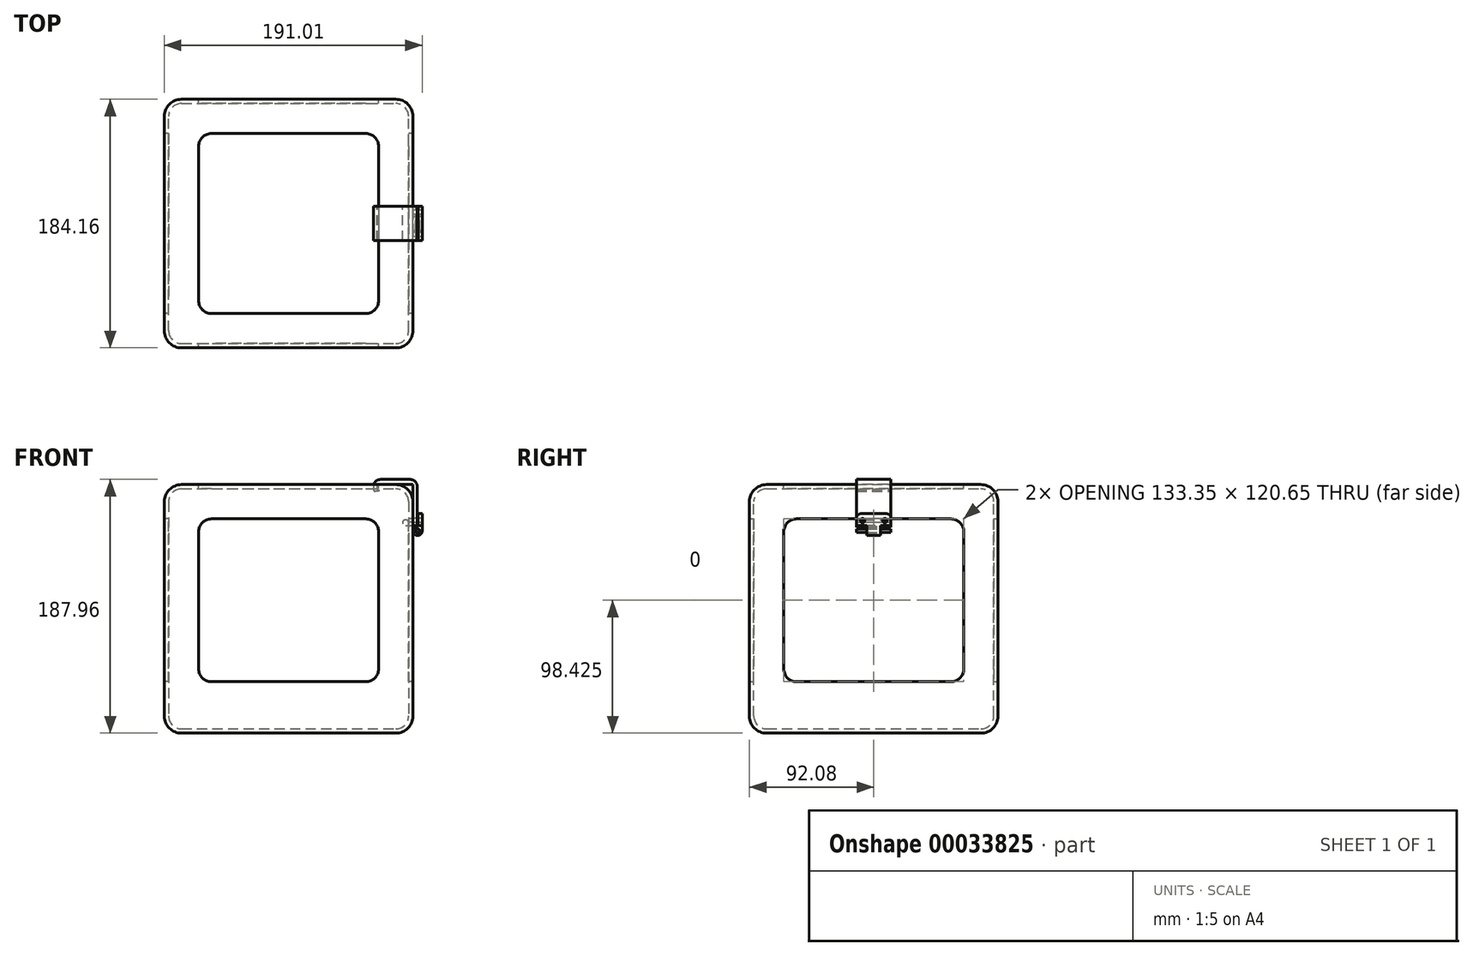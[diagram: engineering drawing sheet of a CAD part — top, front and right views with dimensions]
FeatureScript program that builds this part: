
annotation { "Feature Type Name" : "Feature", "Feature Type Description" : "" }
export const myFeature = defineFeature(function(context is Context, id is Id, definition is map)
    precondition{}
    {
        {
            var Q0;
            Q0=qCreatedBy(makeId("Top.planeOp"),FACE);
            var sketch = newSketch(context, id + "F0", { "sketchPlane" : qUnion([Q0])});
            skLineSegment(sketch, "E0.bottom", {"start": v(-92.08, 92.08) * mm, "end": v(92.08, 92.08) * mm});
            skLineSegment(sketch, "E0.top", {"start": v(-92.08, -92.08) * mm, "end": v(92.08, -92.08) * mm});
            skLineSegment(sketch, "E0.left", {"start": v(-92.08, 92.08) * mm, "end": v(-92.08, -92.08) * mm});
            skLineSegment(sketch, "E0.right", {"start": v(92.08, 92.08) * mm, "end": v(92.08, -92.08) * mm});
            skSolve(sketch);
        }
        {
            var Q0;
            Q0 = qSketchRegion(id + "F0", true);
            extrude(context, id + "F1", {"entities" : qUnion([Q0]), "depth" : 184.15 * mm});
        }
        {
            var Q0;
            Q0=makeQuery(id+"F1.opExtrude","CAP_EDGE",EDGE,{"disambiguationData":[OSD([sQuery(id+"F0.wireOp",EDGE,"E0.top")])],"isStart":false});
            var Q1;
            Q1=makeQuery(id+"F1.opExtrude","CAP_EDGE",EDGE,{"disambiguationData":[OSD([sQuery(id+"F0.wireOp",EDGE,"E0.right")])],"isStart":false});
            var Q2;
            Q2=makeQuery(id+"F1.opExtrude","SWEPT_EDGE",EDGE,{"disambiguationData":[OSD([sQuery(id+"F0.wireOp",EDGE,"E0.top"),sQuery(id+"F0.wireOp",EDGE,"E0.right")])]});
            var Q3;
            Q3=makeQuery(id+"F1.opExtrude","CAP_EDGE",EDGE,{"disambiguationData":[OSD([sQuery(id+"F0.wireOp",EDGE,"E0.left")])],"isStart":false});
            var Q4;
            Q4=makeQuery(id+"F1.opExtrude","SWEPT_EDGE",EDGE,{"disambiguationData":[OSD([sQuery(id+"F0.wireOp",EDGE,"E0.top"),sQuery(id+"F0.wireOp",EDGE,"E0.left")])]});
            var Q5;
            Q5=makeQuery(id+"F1.opExtrude","CAP_EDGE",EDGE,{"disambiguationData":[OSD([sQuery(id+"F0.wireOp",EDGE,"E0.bottom")])],"isStart":false});
            var Q6;
            Q6=makeQuery(id+"F1.opExtrude","SWEPT_EDGE",EDGE,{"disambiguationData":[OSD([sQuery(id+"F0.wireOp",EDGE,"E0.bottom"),sQuery(id+"F0.wireOp",EDGE,"E0.right")])]});
            var Q7;
            Q7=makeQuery(id+"F1.opExtrude","SWEPT_EDGE",EDGE,{"disambiguationData":[OSD([sQuery(id+"F0.wireOp",EDGE,"E0.bottom"),sQuery(id+"F0.wireOp",EDGE,"E0.left")])]});
            var Q8;
            Q8=makeQuery(id+"F1.opExtrude","CAP_EDGE",EDGE,{"disambiguationData":[OSD([sQuery(id+"F0.wireOp",EDGE,"E0.bottom")])],"isStart":true});
            var Q9;
            Q9=makeQuery(id+"F1.opExtrude","CAP_EDGE",EDGE,{"disambiguationData":[OSD([sQuery(id+"F0.wireOp",EDGE,"E0.right")])],"isStart":true});
            var Q10;
            Q10=makeQuery(id+"F1.opExtrude","SWEPT_FACE",FACE,{"disambiguationData":[OSD([sQuery(id+"F0.wireOp",EDGE,"E0.left")])]});
            var Q11;
            Q11=makeQuery(id+"F1.opExtrude","CAP_EDGE",EDGE,{"disambiguationData":[OSD([sQuery(id+"F0.wireOp",EDGE,"E0.top")])],"isStart":true});
            fillet(context, id + "F2", {"entities" : qUnion([Q0, Q1, Q2, Q3, Q4, Q5, Q6, Q7, Q8, Q9, Q10, Q11]), "radius" : 12.7 * mm, "tangentPropagation" : true, "allowEdgeOverflow" : false});
        }
        {
            var Q0;
            Q0=makeQuery(id+"F1.opExtrude","CAP_FACE",FACE,{"disambiguationData":[OSD([sQuery(id+"F0.wireOp",EDGE,"E0.bottom"),sQuery(id+"F0.wireOp",EDGE,"E0.top"),sQuery(id+"F0.wireOp",EDGE,"E0.left"),sQuery(id+"F0.wireOp",EDGE,"E0.right")])],"isStart":false});
            shell(context, id + "F3", {"entities" : qUnion([Q0]), "thickness" : 3.17 * mm});
        }
        {
            var Q0;
            Q0=qCreatedBy(makeId("Right.planeOp"),FACE);
            var sketch = newSketch(context, id + "F4", { "sketchPlane" : qUnion([Q0])});
            skLineSegment(sketch, "E1.bottom", {"start": v(-66.67, 158.75) * mm, "end": v(66.68, 158.75) * mm});
            skLineSegment(sketch, "E1.top", {"start": v(-66.67, 38.1) * mm, "end": v(66.68, 38.1) * mm});
            skLineSegment(sketch, "E1.left", {"start": v(-66.67, 158.75) * mm, "end": v(-66.67, 38.1) * mm});
            skLineSegment(sketch, "E1.right", {"start": v(66.68, 158.75) * mm, "end": v(66.68, 38.1) * mm});
            skSolve(sketch);
        }
        {
            var Q0;
            Q0 = qSketchRegion(id + "F4", true);
            extrude(context, id + "F5", {"entities" : qUnion([Q0]), "operationType" : NewBodyOperationType.REMOVE, "depth" : 127 * mm, "hasSecondDirection" : true, "secondDirectionOppositeDirection" : true, "secondDirectionDepth" : 127 * mm});
        }
        {
            var Q0;
            Q0=qCreatedBy(makeId("Front.planeOp"),FACE);
            var sketch = newSketch(context, id + "F6", { "sketchPlane" : qUnion([Q0])});
            skLineSegment(sketch, "E2.bottom", {"start": v(66.67, 158.75) * mm, "end": v(-66.67, 158.75) * mm});
            skLineSegment(sketch, "E2.top", {"start": v(66.68, 38.1) * mm, "end": v(-66.67, 38.1) * mm});
            skLineSegment(sketch, "E2.left", {"start": v(66.67, 158.75) * mm, "end": v(66.67, 38.1) * mm});
            skLineSegment(sketch, "E2.right", {"start": v(-66.67, 158.75) * mm, "end": v(-66.67, 38.1) * mm});
            skSolve(sketch);
        }
        {
            var Q0;
            Q0 = qSketchRegion(id + "F6", true);
            extrude(context, id + "F7", {"entities" : qUnion([Q0]), "operationType" : NewBodyOperationType.REMOVE, "depth" : 101.6 * mm, "hasSecondDirection" : true, "secondDirectionOppositeDirection" : true, "secondDirectionDepth" : 101.6 * mm});
        }
        {
            var Q0;
            Q0=makeQuery(id+"F7.boolean.opBoolean","COPY",EDGE,{"disambiguationData":[OD(0.0)],"derivedFrom":makeQuery(id+"F7.opExtrude","SWEPT_EDGE",EDGE,{"disambiguationData":[OSD([sQuery(id+"F6.wireOp",EDGE,"E2.bottom"),sQuery(id+"F6.wireOp",EDGE,"E2.left")])]})});
            var Q1;
            Q1=makeQuery(id+"F7.boolean.opBoolean","COPY",EDGE,{"disambiguationData":[OD(0.0)],"derivedFrom":makeQuery(id+"F7.opExtrude","SWEPT_EDGE",EDGE,{"disambiguationData":[OSD([sQuery(id+"F6.wireOp",EDGE,"E2.top"),sQuery(id+"F6.wireOp",EDGE,"E2.left")])]})});
            var Q2;
            Q2=makeQuery(id+"F7.boolean.opBoolean","COPY",EDGE,{"disambiguationData":[OD(0.0)],"derivedFrom":makeQuery(id+"F7.opExtrude","SWEPT_EDGE",EDGE,{"disambiguationData":[OSD([sQuery(id+"F6.wireOp",EDGE,"E2.top"),sQuery(id+"F6.wireOp",EDGE,"E2.right")])]})});
            var Q3;
            Q3=makeQuery(id+"F7.boolean.opBoolean","COPY",EDGE,{"disambiguationData":[OD(0.0)],"derivedFrom":makeQuery(id+"F7.opExtrude","SWEPT_EDGE",EDGE,{"disambiguationData":[OSD([sQuery(id+"F6.wireOp",EDGE,"E2.bottom"),sQuery(id+"F6.wireOp",EDGE,"E2.right")])]})});
            var Q4;
            Q4=makeQuery(id+"F5.boolean.opBoolean","COPY",EDGE,{"disambiguationData":[OD(1.0)],"derivedFrom":makeQuery(id+"F5.opExtrude","SWEPT_EDGE",EDGE,{"disambiguationData":[OSD([sQuery(id+"F4.wireOp",EDGE,"E1.bottom"),sQuery(id+"F4.wireOp",EDGE,"E1.left")])]})});
            var Q5;
            Q5=makeQuery(id+"F5.boolean.opBoolean","COPY",EDGE,{"disambiguationData":[OD(1.0)],"derivedFrom":makeQuery(id+"F5.opExtrude","SWEPT_EDGE",EDGE,{"disambiguationData":[OSD([sQuery(id+"F4.wireOp",EDGE,"E1.bottom"),sQuery(id+"F4.wireOp",EDGE,"E1.right")])]})});
            var Q6;
            Q6=makeQuery(id+"F5.boolean.opBoolean","COPY",EDGE,{"disambiguationData":[OD(1.0)],"derivedFrom":makeQuery(id+"F5.opExtrude","SWEPT_EDGE",EDGE,{"disambiguationData":[OSD([sQuery(id+"F4.wireOp",EDGE,"E1.top"),sQuery(id+"F4.wireOp",EDGE,"E1.left")])]})});
            var Q7;
            Q7=makeQuery(id+"F5.boolean.opBoolean","COPY",EDGE,{"disambiguationData":[OD(1.0)],"derivedFrom":makeQuery(id+"F5.opExtrude","SWEPT_EDGE",EDGE,{"disambiguationData":[OSD([sQuery(id+"F4.wireOp",EDGE,"E1.top"),sQuery(id+"F4.wireOp",EDGE,"E1.right")])]})});
            var Q8;
            Q8=makeQuery(id+"F7.boolean.opBoolean","COPY",EDGE,{"disambiguationData":[OD(1.0)],"derivedFrom":makeQuery(id+"F7.opExtrude","SWEPT_EDGE",EDGE,{"disambiguationData":[OSD([sQuery(id+"F6.wireOp",EDGE,"E2.top"),sQuery(id+"F6.wireOp",EDGE,"E2.left")])]})});
            var Q9;
            Q9=makeQuery(id+"F7.boolean.opBoolean","COPY",EDGE,{"disambiguationData":[OD(1.0)],"derivedFrom":makeQuery(id+"F7.opExtrude","SWEPT_EDGE",EDGE,{"disambiguationData":[OSD([sQuery(id+"F6.wireOp",EDGE,"E2.bottom"),sQuery(id+"F6.wireOp",EDGE,"E2.left")])]})});
            var Q10;
            Q10=makeQuery(id+"F7.boolean.opBoolean","COPY",EDGE,{"disambiguationData":[OD(1.0)],"derivedFrom":makeQuery(id+"F7.opExtrude","SWEPT_EDGE",EDGE,{"disambiguationData":[OSD([sQuery(id+"F6.wireOp",EDGE,"E2.bottom"),sQuery(id+"F6.wireOp",EDGE,"E2.right")])]})});
            var Q11;
            Q11=makeQuery(id+"F7.boolean.opBoolean","COPY",EDGE,{"disambiguationData":[OD(1.0)],"derivedFrom":makeQuery(id+"F7.opExtrude","SWEPT_EDGE",EDGE,{"disambiguationData":[OSD([sQuery(id+"F6.wireOp",EDGE,"E2.top"),sQuery(id+"F6.wireOp",EDGE,"E2.right")])]})});
            var Q12;
            Q12=makeQuery(id+"F5.boolean.opBoolean","COPY",EDGE,{"disambiguationData":[OD(0.0)],"derivedFrom":makeQuery(id+"F5.opExtrude","SWEPT_EDGE",EDGE,{"disambiguationData":[OSD([sQuery(id+"F4.wireOp",EDGE,"E1.top"),sQuery(id+"F4.wireOp",EDGE,"E1.left")])]})});
            var Q13;
            Q13=makeQuery(id+"F5.boolean.opBoolean","COPY",EDGE,{"disambiguationData":[OD(0.0)],"derivedFrom":makeQuery(id+"F5.opExtrude","SWEPT_EDGE",EDGE,{"disambiguationData":[OSD([sQuery(id+"F4.wireOp",EDGE,"E1.bottom"),sQuery(id+"F4.wireOp",EDGE,"E1.left")])]})});
            var Q14;
            Q14=makeQuery(id+"F5.boolean.opBoolean","COPY",EDGE,{"disambiguationData":[OD(0.0)],"derivedFrom":makeQuery(id+"F5.opExtrude","SWEPT_EDGE",EDGE,{"disambiguationData":[OSD([sQuery(id+"F4.wireOp",EDGE,"E1.bottom"),sQuery(id+"F4.wireOp",EDGE,"E1.right")])]})});
            var Q15;
            Q15=makeQuery(id+"F5.boolean.opBoolean","COPY",EDGE,{"disambiguationData":[OD(0.0)],"derivedFrom":makeQuery(id+"F5.opExtrude","SWEPT_EDGE",EDGE,{"disambiguationData":[OSD([sQuery(id+"F4.wireOp",EDGE,"E1.top"),sQuery(id+"F4.wireOp",EDGE,"E1.right")])]})});
            fillet(context, id + "F8", {"entities" : qUnion([Q0, Q1, Q2, Q3, Q4, Q5, Q6, Q7, Q8, Q9, Q10, Q11, Q12, Q13, Q14, Q15]), "radius" : 9.52 * mm, "tangentPropagation" : true, "allowEdgeOverflow" : false});
        }
        {
            var Q0;
            Q0=qCreatedBy(makeId("Top.planeOp"),FACE);
            cPlane(context, id + "F9", {"entities" : qUnion([Q0]), "cplaneType" : CPlaneType.OFFSET, "offset" : 184.15 * mm, "width" : 152.4 * mm, "height" : 152.4 * mm});
        }
        {
            var Q0;
            Q0=qCreatedBy(id+"F9.planeOp",FACE);
            var sketch = newSketch(context, id + "F10", { "sketchPlane" : qUnion([Q0])});
            skLineSegment(sketch, "E3.bottom", {"start": v(-66.67, 66.67) * mm, "end": v(66.67, 66.67) * mm});
            skLineSegment(sketch, "E3.top", {"start": v(-66.67, -66.67) * mm, "end": v(66.68, -66.67) * mm});
            skLineSegment(sketch, "E3.left", {"start": v(-66.67, 66.67) * mm, "end": v(-66.67, -66.67) * mm});
            skLineSegment(sketch, "E3.right", {"start": v(66.67, 66.67) * mm, "end": v(66.68, -66.67) * mm});
            skLineSegment(sketch, "E4.bottom", {"start": v(-79.38, 79.38) * mm, "end": v(79.38, 79.38) * mm});
            skLineSegment(sketch, "E4.top", {"start": v(-79.37, -79.38) * mm, "end": v(79.38, -79.38) * mm});
            skLineSegment(sketch, "E4.left", {"start": v(-79.38, 79.38) * mm, "end": v(-79.37, -79.38) * mm});
            skLineSegment(sketch, "E4.right", {"start": v(79.38, 79.38) * mm, "end": v(79.38, -79.38) * mm});
            skSolve(sketch);
        }
        {
            var Q0;
            Q0=makeQuery(id+"F10.imprint","IMPRINT",FACE,{"disambiguationData":[TD([[makeQuery(id+"F10.imprint","IMPRINT",EDGE,{"derivedFrom":sQuery(id+"F10.wireOp",EDGE,"E3.bottom")}),1.0]])]});
            extrude(context, id + "F11", {"entities" : qUnion([Q0]), "operationType" : NewBodyOperationType.ADD, "oppositeDirection" : true, "depth" : 3.17 * mm});
        }
        {
            var Q0;
            Q0=makeQuery(id+"F11.opExtrude","SWEPT_EDGE",EDGE,{"disambiguationData":[OSD([sQuery(id+"F10.wireOp",EDGE,"E3.bottom"),sQuery(id+"F10.wireOp",EDGE,"E3.left")])]});
            var Q1;
            Q1=makeQuery(id+"F11.opExtrude","SWEPT_EDGE",EDGE,{"disambiguationData":[OSD([sQuery(id+"F10.wireOp",EDGE,"E3.top"),sQuery(id+"F10.wireOp",EDGE,"E3.left")])]});
            var Q2;
            Q2=makeQuery(id+"F11.opExtrude","SWEPT_EDGE",EDGE,{"disambiguationData":[OSD([sQuery(id+"F10.wireOp",EDGE,"E3.bottom"),sQuery(id+"F10.wireOp",EDGE,"E3.right")])]});
            var Q3;
            Q3=makeQuery(id+"F11.opExtrude","SWEPT_EDGE",EDGE,{"disambiguationData":[OSD([sQuery(id+"F10.wireOp",EDGE,"E3.top"),sQuery(id+"F10.wireOp",EDGE,"E3.right")])]});
            fillet(context, id + "F12", {"entities" : qUnion([Q0, Q1, Q2, Q3]), "radius" : 9.52 * mm, "tangentPropagation" : true, "allowEdgeOverflow" : false});
        }
        {
            var Q0;
            Q0=qCreatedBy(makeId("Right.planeOp"),FACE);
            cPlane(context, id + "F13", {"entities" : qUnion([Q0]), "cplaneType" : CPlaneType.OFFSET, "offset" : 92.07 * mm, "width" : 152.4 * mm, "height" : 152.4 * mm});
        }
        {
            var Q0;
            Q0=qCreatedBy(id+"F13.planeOp",FACE);
            var sketch = newSketch(context, id + "F14", { "sketchPlane" : qUnion([Q0])});
            skLineSegment(sketch, "E5.bottom", {"start": v(-19.05, 190.5) * mm, "end": v(19.05, 190.5) * mm});
            skLineSegment(sketch, "E5.top", {"start": v(-19.05, 146.05) * mm, "end": v(19.05, 146.05) * mm});
            skLineSegment(sketch, "E5.left", {"start": v(-19.05, 190.5) * mm, "end": v(-19.05, 146.05) * mm});
            skLineSegment(sketch, "E5.right", {"start": v(19.05, 190.5) * mm, "end": v(19.05, 146.05) * mm});
            skLineSegment(sketch, "E6", {"start": v(0, 190.5) * mm, "end": v(0, 146.05) * mm, "construction": true});
            skLineSegment(sketch, "E7", {"start": v(0, 146.05) * mm, "end": v(0, 0) * mm, "construction": true});
            skCircle(sketch, "E8", {"center": v(8.25, 157.48) * mm, "radius": 1.59 * mm});
            skCircle(sketch, "E9", {"center": v(-8.26, 157.48) * mm, "radius": 1.59 * mm});
            skLineSegment(sketch, "E10", {"start": v(-8.26, 157.48) * mm, "end": v(8.25, 157.48) * mm, "construction": true});
            skSolve(sketch);
        }
        {
            var Q0;
            Q0=qCreatedBy(makeId("Front.planeOp"),FACE);
            var sketch = newSketch(context, id + "F15", { "sketchPlane" : qUnion([Q0])});
            skLineSegment(sketch, "E11", {"start": v(95.25, 187.96) * mm, "end": v(62.86, 187.96) * mm});
            skLineSegment(sketch, "E12", {"start": v(62.86, 187.96) * mm, "end": v(62.86, 184.15) * mm});
            skLineSegment(sketch, "E13", {"start": v(62.86, 184.15) * mm, "end": v(92.08, 184.15) * mm});
            skLineSegment(sketch, "E14", {"start": v(92.07, 184.15) * mm, "end": v(92.08, 149.86) * mm});
            skLineSegment(sketch, "E15", {"start": v(92.08, 149.86) * mm, "end": v(95.25, 149.86) * mm});
            skLineSegment(sketch, "E16", {"start": v(95.25, 149.86) * mm, "end": v(95.25, 187.96) * mm});
            skLineSegment(sketch, "E17", {"start": v(65.4, 184.15) * mm, "end": v(65.4, 180.85) * mm});
            skLineSegment(sketch, "E18", {"start": v(65.4, 180.85) * mm, "end": v(66.86, 180.21) * mm});
            skLineSegment(sketch, "E19", {"start": v(66.86, 180.21) * mm, "end": v(66.17, 179.07) * mm});
            skLineSegment(sketch, "E20", {"start": v(66.17, 179.07) * mm, "end": v(62.86, 179.07) * mm});
            skLineSegment(sketch, "E21", {"start": v(62.86, 179.07) * mm, "end": v(62.86, 184.15) * mm});
            skLineSegment(sketch, "E22", {"start": v(92.08, 156.21) * mm, "end": v(88.77, 156.21) * mm});
            skLineSegment(sketch, "E23", {"start": v(88.77, 156.21) * mm, "end": v(88.12, 159.07) * mm});
            skLineSegment(sketch, "E24", {"start": v(88.12, 159.07) * mm, "end": v(86.85, 159.07) * mm});
            skLineSegment(sketch, "E25", {"start": v(86.85, 159.07) * mm, "end": v(86.59, 155.88) * mm});
            skLineSegment(sketch, "E26", {"start": v(86.59, 155.88) * mm, "end": v(86.59, 153.67) * mm});
            skLineSegment(sketch, "E27", {"start": v(86.59, 153.67) * mm, "end": v(92.08, 153.67) * mm});
            skLineSegment(sketch, "E28.bottom", {"start": v(95.76, 149.86) * mm, "end": v(98.93, 149.86) * mm});
            skLineSegment(sketch, "E28.top", {"start": v(95.76, 162.56) * mm, "end": v(98.93, 162.56) * mm});
            skLineSegment(sketch, "E28.left", {"start": v(95.76, 149.86) * mm, "end": v(95.76, 162.56) * mm});
            skLineSegment(sketch, "E28.right", {"start": v(98.93, 149.86) * mm, "end": v(98.93, 162.56) * mm});
            skLineSegment(sketch, "E29", {"start": v(95.25, 149.86) * mm, "end": v(95.76, 149.86) * mm});
            skCircle(sketch, "E30", {"center": v(95.5, 149.86) * mm, "radius": 3.43 * mm});
            skCircle(sketch, "E31", {"center": v(86.59, 155.88) * mm, "radius": 2.2 * mm});
            skSolve(sketch);
        }
        {
            var Q0;
            Q0=qCreatedBy(makeId("Front.planeOp"),FACE);
            var sketch = newSketch(context, id + "F16", { "sketchPlane" : qUnion([Q0])});
            skLineSegment(sketch, "E32.0", {"start": v(95.25, 187.96) * mm, "end": v(62.86, 187.96) * mm});
            skLineSegment(sketch, "E32.1", {"start": v(62.86, 187.96) * mm, "end": v(62.86, 184.15) * mm});
            skLineSegment(sketch, "E32.2", {"start": v(65.4, 184.15) * mm, "end": v(92.08, 184.15) * mm});
            skLineSegment(sketch, "E32.3", {"start": v(92.07, 184.15) * mm, "end": v(92.08, 156.21) * mm});
            skLineSegment(sketch, "E32.5", {"start": v(95.25, 153.28) * mm, "end": v(95.25, 187.96) * mm});
            skLineSegment(sketch, "E32.6", {"start": v(65.4, 184.15) * mm, "end": v(65.4, 180.85) * mm});
            skLineSegment(sketch, "E32.7", {"start": v(65.4, 180.85) * mm, "end": v(66.86, 180.21) * mm});
            skLineSegment(sketch, "E32.8", {"start": v(66.86, 180.21) * mm, "end": v(66.17, 179.07) * mm});
            skLineSegment(sketch, "E32.9", {"start": v(66.17, 179.07) * mm, "end": v(62.86, 179.07) * mm});
            skLineSegment(sketch, "E32.10", {"start": v(62.86, 179.07) * mm, "end": v(62.86, 184.15) * mm});
            skLineSegment(sketch, "E32.11", {"start": v(92.08, 156.21) * mm, "end": v(88.77, 156.21) * mm});
            skLineSegment(sketch, "E32.16", {"start": v(86.59, 153.67) * mm, "end": v(92.08, 153.67) * mm});
            skPoint(sketch, "E33.orphan", {"position": v(62.86, 184.15) * mm});
            skLineSegment(sketch, "E34.trimOffspring", {"start": v(92.08, 153.67) * mm, "end": v(92.08, 149.86) * mm});
            skArc(sketch, "E35.0", {"start": v(92.08, 149.86) * mm, "mid": v(98.02, 147.53) * mm, "end": v(95.25, 153.28) * mm});
            skPoint(sketch, "E32.4.end.orphan", {"position": v(95.25, 149.86) * mm});
            skPoint(sketch, "E32.4.start.orphan", {"position": v(92.08, 149.86) * mm});
            skCircle(sketch, "E36", {"center": v(95.5, 149.86) * mm, "radius": 1.59 * mm});
            skArc(sketch, "E37.0", {"start": v(88.77, 156.21) * mm, "mid": v(84.91, 157.32) * mm, "end": v(86.59, 153.67) * mm});
            skSolve(sketch);
        }
        {
            var Q0;
            Q0 = qSketchRegion(id + "F16", true);
            extrude(context, id + "F17", {"entities" : qUnion([Q0]), "endBound" : BoundingType.SYMMETRIC, "depth" : 25.4 * mm});
        }
        {
            var Q0;
            Q0=makeQuery(id+"F17.opExtrude","SWEPT_EDGE",EDGE,{"disambiguationData":[OSD([sQuery(id+"F16.wireOp",EDGE,"E32.13"),sQuery(id+"F16.wireOp",EDGE,"E32.14")])]});
            var Q1;
            Q1=makeQuery(id+"F17.opExtrude","SWEPT_EDGE",EDGE,{"disambiguationData":[OSD([sQuery(id+"F16.wireOp",EDGE,"E32.15"),sQuery(id+"F16.wireOp",EDGE,"E32.16")])]});
            var Q2;
            Q2=makeQuery(id+"F17.opExtrude","SWEPT_EDGE",EDGE,{"disambiguationData":[OSD([sQuery(id+"F16.wireOp",EDGE,"E32.9"),sQuery(id+"F16.wireOp",EDGE,"E32.10")])]});
            fillet(context, id + "F18", {"entities" : qUnion([Q0, Q1, Q2]), "radius" : 1.27 * mm, "tangentPropagation" : true, "allowEdgeOverflow" : false});
        }
        {
            var Q0;
            Q0=makeQuery(id+"F17.opExtrude","SWEPT_EDGE",EDGE,{"disambiguationData":[OSD([sQuery(id+"F16.wireOp",EDGE,"E32.0"),sQuery(id+"F16.wireOp",EDGE,"E32.1")])]});
            var Q1;
            Q1=makeQuery(id+"F17.opExtrude","SWEPT_EDGE",EDGE,{"disambiguationData":[OSD([sQuery(id+"F16.wireOp",EDGE,"E32.0"),sQuery(id+"F16.wireOp",EDGE,"E32.5")])]});
            fillet(context, id + "F19", {"entities" : qUnion([Q0, Q1]), "radius" : 5.08 * mm, "tangentPropagation" : true, "allowEdgeOverflow" : false});
        }
        {
            var Q0;
            Q0=makeQuery(id+"F14.imprint","IMPRINT",FACE,{"disambiguationData":[TD([[makeQuery(id+"F14.imprint","IMPRINT",EDGE,{"derivedFrom":sQuery(id+"F14.wireOp",EDGE,"E5.bottom")}),-1.0]])]});
            var sketch = newSketch(context, id + "F20", { "sketchPlane" : qUnion([Q0])});
            skLineSegment(sketch, "E38.bottom", {"start": v(5.79, 153.67) * mm, "end": v(-5.79, 153.67) * mm});
            skLineSegment(sketch, "E38.top", {"start": v(5.79, 146.05) * mm, "end": v(-5.79, 146.05) * mm});
            skLineSegment(sketch, "E38.left", {"start": v(5.79, 153.67) * mm, "end": v(5.79, 146.05) * mm});
            skLineSegment(sketch, "E38.right", {"start": v(-5.79, 153.67) * mm, "end": v(-5.79, 146.05) * mm});
            skSolve(sketch);
        }
        {
            var Q0;
            Q0 = qSketchRegion(id + "F20", true);
            extrude(context, id + "F21", {"entities" : qUnion([Q0]), "operationType" : NewBodyOperationType.REMOVE, "depth" : 25.4 * mm});
        }
        {
            var Q0;
            Q0=qCreatedBy(makeId("Front.planeOp"),FACE);
            var sketch = newSketch(context, id + "F22", { "sketchPlane" : qUnion([Q0])});
            skLineSegment(sketch, "E39.0", {"start": v(95.76, 162.56) * mm, "end": v(98.93, 162.56) * mm});
            skLineSegment(sketch, "E40.0", {"start": v(98.93, 149.86) * mm, "end": v(98.93, 162.56) * mm});
            skLineSegment(sketch, "E41.0", {"start": v(95.76, 153.28) * mm, "end": v(95.76, 162.56) * mm});
            skArc(sketch, "E42.0", {"start": v(95.76, 153.28) * mm, "mid": v(93, 147.53) * mm, "end": v(98.93, 149.86) * mm});
            skPoint(sketch, "E43.orphan", {"position": v(95.76, 149.86) * mm});
            skCircle(sketch, "E44.0", {"center": v(95.5, 149.86) * mm, "radius": 1.59 * mm});
            skSolve(sketch);
        }
        {
            var Q0;
            Q0 = qSketchRegion(id + "F22", true);
            extrude(context, id + "F23", {"entities" : qUnion([Q0]), "endBound" : BoundingType.SYMMETRIC, "depth" : 25.4 * mm});
        }
        {
            var Q0;
            Q0=makeQuery(id+"F14.imprint","IMPRINT",FACE,{"disambiguationData":[TD([[makeQuery(id+"F14.imprint","IMPRINT",EDGE,{"derivedFrom":sQuery(id+"F14.wireOp",EDGE,"E5.bottom")}),-1.0]])]});
            var sketch = newSketch(context, id + "F24", { "sketchPlane" : qUnion([Q0])});
            skLineSegment(sketch, "E45.bottom", {"start": v(5.15, 153.67) * mm, "end": v(13.32, 153.67) * mm});
            skLineSegment(sketch, "E45.top", {"start": v(5.15, 145.79) * mm, "end": v(13.32, 145.79) * mm});
            skLineSegment(sketch, "E45.left", {"start": v(5.15, 153.67) * mm, "end": v(5.15, 145.79) * mm});
            skLineSegment(sketch, "E45.right", {"start": v(13.32, 153.67) * mm, "end": v(13.32, 145.79) * mm});
            skLineSegment(sketch, "E46.bottom", {"start": v(-5.15, 153.67) * mm, "end": v(-13.35, 153.67) * mm});
            skLineSegment(sketch, "E46.top", {"start": v(-5.15, 145.79) * mm, "end": v(-13.35, 145.79) * mm});
            skLineSegment(sketch, "E46.left", {"start": v(-5.15, 153.67) * mm, "end": v(-5.15, 145.79) * mm});
            skLineSegment(sketch, "E46.right", {"start": v(-13.35, 153.67) * mm, "end": v(-13.35, 145.79) * mm});
            skCircle(sketch, "E47.0", {"center": v(-8.26, 157.48) * mm, "radius": 1.59 * mm});
            skCircle(sketch, "E48.0", {"center": v(8.25, 157.48) * mm, "radius": 1.59 * mm});
            skSolve(sketch);
        }
        {
            var Q0;
            Q0 = qSketchRegion(id + "F24", true);
            extrude(context, id + "F25", {"entities" : qUnion([Q0]), "operationType" : NewBodyOperationType.REMOVE, "depth" : 25.4 * mm});
        }
        {
            var Q0;
            Q0=makeQuery(id+"F23.opExtrude","CAP_EDGE",EDGE,{"disambiguationData":[OSD([sQuery(id+"F22.wireOp",EDGE,"E39.0")])],"isStart":false});
            var Q1;
            Q1=makeQuery(id+"F23.opExtrude","CAP_EDGE",EDGE,{"disambiguationData":[OSD([sQuery(id+"F22.wireOp",EDGE,"E39.0")])],"isStart":true});
            fillet(context, id + "F26", {"entities" : qUnion([Q0, Q1]), "radius" : 3.17 * mm, "tangentPropagation" : true, "allowEdgeOverflow" : false});
        }
        {
            var Q0;
            Q0=qCreatedBy(makeId("Front.planeOp"),FACE);
            var sketch = newSketch(context, id + "F27", { "sketchPlane" : qUnion([Q0])});
            skCircle(sketch, "E49", {"center": v(95.5, 149.86) * mm, "radius": 1.27 * mm});
            skSolve(sketch);
        }
        {
            var Q0;
            Q0 = qSketchRegion(id + "F27", true);
            extrude(context, id + "F28", {"entities" : qUnion([Q0]), "endBound" : BoundingType.SYMMETRIC, "depth" : 25.4 * mm});
        }
    });
